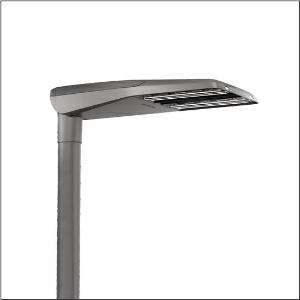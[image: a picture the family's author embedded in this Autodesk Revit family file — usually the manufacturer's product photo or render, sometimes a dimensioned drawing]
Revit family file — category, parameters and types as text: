
# Revit family: streetlight_sl_11_iq_midi___st1_0p1_0_5xc3k51g08me_2a46
name_source: partatom
category: Lighting Fixtures
units: mm (PartAtom-declared; Revit-internal decimal feet)

## family parameters
Cut with Voids When Loaded = No
Host = Face
Light Source = No
Part Type = Normal
Room Calculation Point = No
Round Connector Dimension = Use Diameter
Shared = No

## types (1)
- --- (1 x LED, 9410 lm, 63 W, 3000K)
    Apparent Load = 63 VA
    CIE Flux Codes = 32 65 95 100 100
    Color Rendering = 70
    Color Temperature = 3000K
    Default Elevation = 1800 mm
    Description = Streetlight SL 11 iQ midi, mast luminaire, primary light control with 3 zone facetted reflector, of plastic, silver coated, highly specular, primary optical cover: cover, of PMMA, transparent, light distribution: ST1.0P1.0, light emission: direct distribution, primary light characteristic: asymmetric, installation type: post-top, side-entry, LED, High Power LED, rated luminous flux: 9.410lm, luminous efficacy: 149lm/W, light colour: 730, colour temperature: 3000K, control: Street-Remote, Auto-Match, Temp-Guard, Lumen-Switch, Night-Set, Smart-Wire, Light-Fading, Desk-Remote (wireless, voltage-free reading and setting of iQ features in the workshop via application-optimized NFC function/RFID function), optimised constant luminous flux control (CLO 2.0), presetting dimming linear, with cable H07RN-F 5x 1.5mm², mains connection: 230..240V, AC, 50/60Hz, connection cable pre-assembled, cable length: 12,5m, start of lifetime: 63W, end of service life: 67W, reduction: 30W, luminaire housing, of diecast aluminium, powder-coated, Siteco® metallic grey (DB 702S), please order mast flange separately, inclination adjustable without tools: 0°, 5°, 10°, 15° (post-top) | 0°, -5°, -10°, -15° (side-entry), sealing non-destructively replaceable, multi-level sealing system, length: 780mm, width: 376mm, height: 118mm, mast flange for spigot size: 42mm (side-entry): 5XC10008XM4, 60/48mm (side-entry/post-top): 5XC10108XM2, 76/60mm (side-entry/post-top): 5XC10108XM1, equipment: Power, protection rating (complete): IP66, insulation class (complete): insulation class II (safety insulation), certification: CE, ENEC, VDE, impact resistance: IK09, permissible operating ambient temperature for outdoor applications: -25..+50°C, standard-compliant lighting for roads and squares, Environmental Product Declaration (EPD) tested and certified by an independent institute, packaging unit: 1 piece

Light Distribution: ST1.0P1.0
    Height = 118 mm
    Lamp = 1 x LED
    Lamp Light Flux = 9410 lm
    Lamp Power = 63 W
    Lamp count = 1
    Length = 780 mm
    Luminous efficacy = 149 lm/W
    Manufacturer = Siteco
    ModVariant = No
    Model = 5XC3K51G08ME
    Number of Poles = 1
    OnlyDefault = Yes
    Power Factor = 1
    Product Name = Streetlight SL 11 iQ midi | ST1.0P1.0
    Product group = mast luminaire | pylon top
    ProductGroupID = 6100
    Protection Class = Protection class II
    Protection Degree = IP 66
    RLX_Detail_Level = 1
    RLX_Emergency_Light_Flux = 0 lm
    RLX_Emergency_Type = 0
    RLX_Emergency_Type_DB = No
    RlxData = <blob elided: 70721 chars, md5=5232b5bb>
    Socket = socket
    Standby Power = 0 W
    System Light Flux = 9410 lm
    System Power = 63 W
    Type Comments = factory setting: luminous flux: 100 % | dim-lin: 254 | 553 mA
    Type Image = l_1005960.jpg
    URL = http://relux.com
    VarID = @adj_003295
    Voltage = 0 V
    Weight = 0.00 kg
    Width = 376 mm

## geometry (parser evidence)
native form markers: Blend x4, Sweep x10
no freeform markers — native parametric forms only
